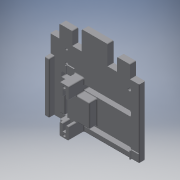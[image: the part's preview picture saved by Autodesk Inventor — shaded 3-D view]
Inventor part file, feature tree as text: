
AUTODESK INVENTOR PART (.ipt)
format: ipt  version: 2018 (Build 220112000, 112)  size: 937,984 bytes
history: native  units: in
note: dims shown in document units (in); Inventor stores cm internally (conversion verified against a paired STEP export)
features: reference x27, extrude x14, sketch x14, other x11, fillet x8, plane x6, projected_geometry x4
ambient origin geometry x8: Origin, YZ Plane, XZ Plane, XY Plane, X Axis, Y Axis, Z Axis, Center Point
bodies: Solid1 (feature_tree)
feature tree (84):
  extrude  "Extrusion1"  Depth=0.2839in
  sketch  "Sketch2"  dims[d6=0.2839in d7=2.1654in]
  plane  "Work Plane1"
  extrude  "Extrusion2"  Depth=2.1654in
  extrude  "Extrusion3"  Depth=0.1969in
  sketch  "Sketch4"  dims[d12=0.1969in d14=0.1181in d15=0.0in]
  plane  "Work Plane2"
  extrude  "Extrusion4"  Depth=0.1181in TaperAngle=0.0deg
  sketch  "Sketch5"  dims[d16=0.0098in d17=0.1969in]
  plane  "Work Plane3"
  extrude  "Extrusion5"  Depth=0.1969in
  sketch  "Sketch6"  dims[d18=1.0in d19=0.0in d20=0.1969in d21=0.0in]
  plane  "Work Plane4"
  extrude  "Extrusion6"  Depth=0.1969in TaperAngle=0.0deg
  sketch  "Sketch7"  dims[d22=0.0098in d23=2.0in]
  plane  "Work Plane5"
  extrude  "Extrusion7"  Depth=0.0098in
  sketch  "Sketch8"  dims[d24=0.1969in d25=0.0in d27=0.1969in d28=0.0098in d29=0.0098in d30=0.0692in d31=0.1181in d32=0.1969in d33=0.0in]
  plane  "Work Plane6"
  extrude  "Extrusion8"  Depth=0.1969in
  fillet  "Fillet1"  Radius=0.0098in
  fillet  "Fillet4"  Radius=0.0098in
  fillet  "Fillet5"  Radius=0.0692in
  fillet  "Fillet6"  Radius=0.1181in
  fillet  "Fillet7"  Radius=0.1969in
  extrude  "Extrusion9"  Depth=0.1969in TaperAngle=0.0deg
  extrude  "Extrusion10"  Depth=0.0098in
  fillet  "Fillet8"  Radius=0.1575in
  extrude  "Extrusion11"  Depth=0.0098in
  fillet  "Fillet9"  Radius=0.1575in
  extrude  "Extrusion12"  Depth=0.0787in
  extrude  "Extrusion13"  Depth=0.0787in
  fillet  "Fillet10"  Radius=0.0787in
  extrude  "Extrusion14"  Depth=0.0394in
  sketch  "Sketch1"  dims[d3=1.0236in d5=0.2839in]
  reference  "Reference2"
  reference  "Reference3"
  sketch  "Sketch3"  dims[d8=0.1969in d9=0.1969in]
  projected_geometry  "Projected Loop1"
  reference  "Reference4"
  reference  "Reference5"
  reference  "Reference6"
  reference  "Reference7"
  reference  "Reference8"
  reference  "Reference9"
  reference  "Reference10"
  reference  "Reference11"
  reference  "Reference12"
  reference  "Reference13"
  reference  "Reference14"
  reference  "Reference15"
  reference  "Reference16"
  reference  "Reference17"
  reference  "Reference18"
  reference  "Reference19"
  reference  "Reference20"
  reference  "Reference21"
  sketch  "Sketch9"  dims[d34=0.1969in d35=0.0in d36=0.1969in d37=0.0in]
  sketch  "Sketch10"  dims[d38=0.0098in d39=0.0098in d42=0.1575in]
  reference  "Reference22"
  projected_geometry  "Projected Loop2"
  sketch  "Sketch11"  dims[d43=0.0098in d44=0.0098in d45=0.1575in]
  sketch  "Sketch12"  dims[d46=0.0787in d48=0.0787in]
  projected_geometry  "Projected Loop3"
  projected_geometry  "Projected Loop4"
  sketch  "Sketch14"  dims[d49=0.0787in d50=0.0787in d51=0.0787in]
  reference  "Reference23"
  reference  "Reference24"
  reference  "Reference25"
  reference  "Reference26"
  reference  "Reference27"
  reference  "Reference28"
  sketch  "Sketch15"  dims[d52=0.1969in d53=0.0in d54=0.0394in d57=0.0394in d58=0.0394in d59=0.0394in d60=0.0394in d61=1.0in d62=0.5in d63=0.0in d64=0.0in d65=0.1181in d66=0.0in d67=0.0394in d68=0.5in d69=1.0in d70=0.75in d71=0.25in d72=0.5in d73=0.5in d74=1.0in d75=0.0in d76=0.0394in d77=0.1969in d78=0.0in d79=0.0098in d80=0.0394in d81=0.0098in d82=0.0394in d83=0.0098in d84=0.0394in d85=0.0098in d86=0.0394in d87=0.0394in d88=0.0in d89=0.0098in d90=0.3937in d91=0.0in]
  other  "<userpath>\OneDrive\Documents\Inventor\TSA\2018\Animatronics\Tortoise\TurtleAssembly2.iam"
  other  "TurtleAssembly2.iam"
  other  "arduino uno:3"
  other  "PCB_Final_Default:1"
  other  "HeadOpenRack:3"
  other  "servo (2):9"
  other  "Frame - Copy:1"
  other  "SyringeAttachment:7"
  other  "HeadOpenRack:4"
  other  "TableLeg:2"
  other  "TableLeg:1"
